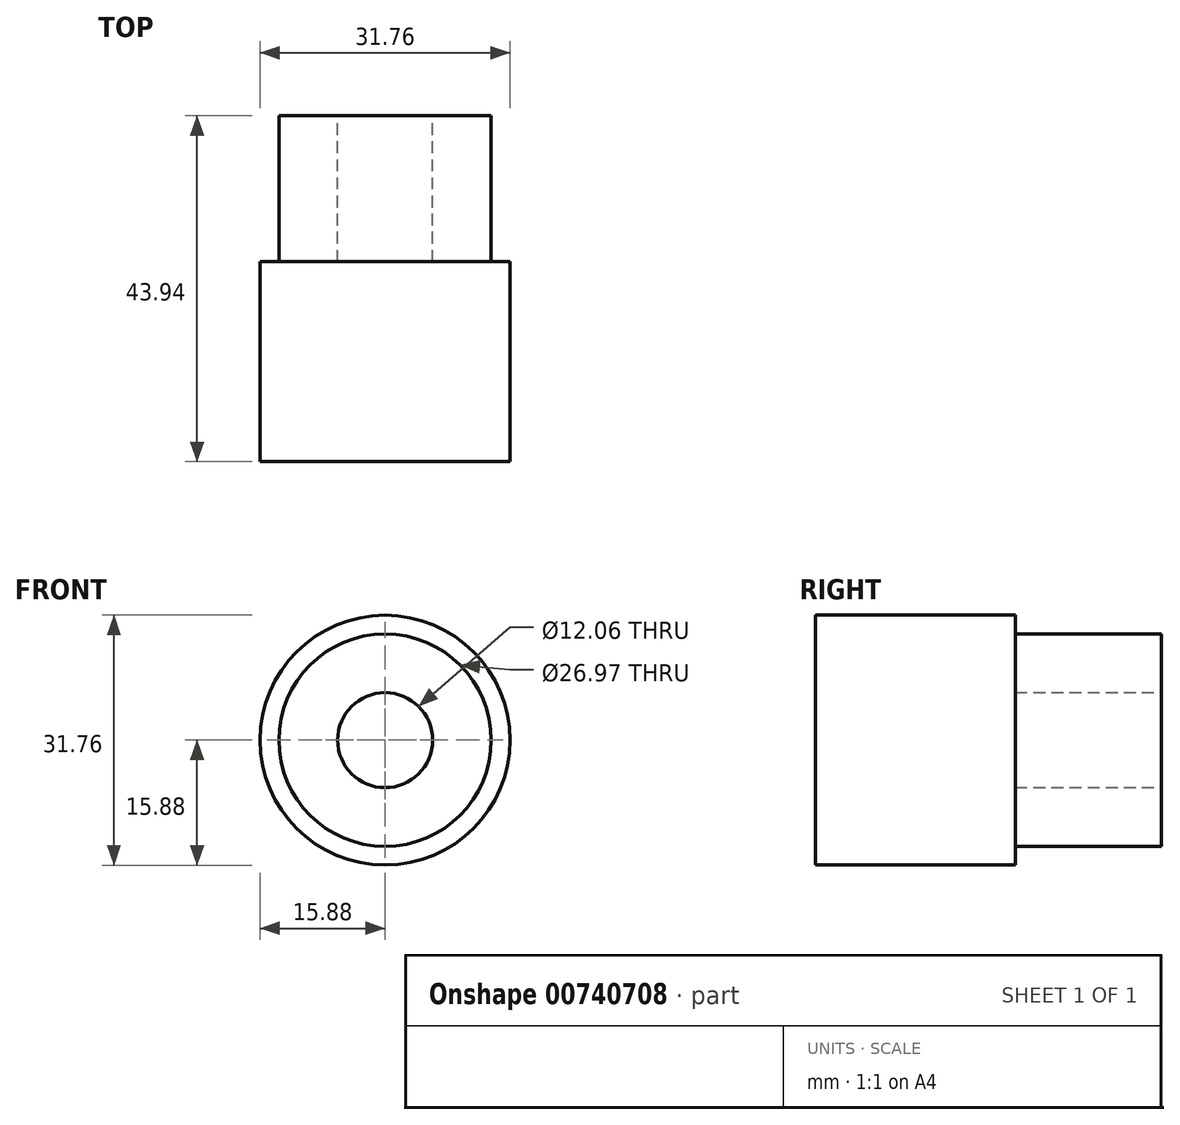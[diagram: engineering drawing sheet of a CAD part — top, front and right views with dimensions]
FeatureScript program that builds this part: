
annotation { "Feature Type Name" : "Feature", "Feature Type Description" : "" }
export const myFeature = defineFeature(function(context is Context, id is Id, definition is map)
    precondition{}
    {
        {
            var Q0;
            Q0=qCreatedBy(makeId("Front.planeOp"),FACE);
            var sketch = newSketch(context, id + "F0", { "sketchPlane" : qUnion([Q0])});
            skCircle(sketch, "E0", {"center": v(0, 0) * mm, "radius": 15.88 * mm});
            skSolve(sketch);
        }
        {
            var Q0;
            Q0=sQuery(id+"F0.wireOp",EDGE,"E0");
            extrude(context, id + "F1", {"bodyType" : ToolBodyType.SURFACE, "surfaceEntities" : qUnion([Q0]), "depth" : 25.4 * mm, "offsetDistance" : 25.4 * mm});
        }
        {
            var Q0;
            Q0=qCreatedBy(makeId("Front.planeOp"),FACE);
            var sketch = newSketch(context, id + "F2", { "sketchPlane" : qUnion([Q0])});
            skCircle(sketch, "E1", {"center": v(0, 0) * mm, "radius": 13.49 * mm});
            skSolve(sketch);
        }
        {
            var Q0;
            Q0=sQuery(id+"F2.wireOp",EDGE,"E1");
            extrude(context, id + "F3", {"bodyType" : ToolBodyType.SURFACE, "surfaceEntities" : qUnion([Q0]), "oppositeDirection" : true, "depth" : 18.54 * mm, "offsetDistance" : 25.4 * mm});
        }
        {
            var Q0;
            Q0=qCreatedBy(makeId("Front.planeOp"),FACE);
            var sketch = newSketch(context, id + "F4", { "sketchPlane" : qUnion([Q0])});
            skCircle(sketch, "E2", {"center": v(0, 0) * mm, "radius": 6.03 * mm});
            skSolve(sketch);
        }
        {
            var Q0;
            Q0=sQuery(id+"F4.wireOp",EDGE,"E2");
            extrude(context, id + "F5", {"bodyType" : ToolBodyType.SURFACE, "surfaceEntities" : qUnion([Q0]), "oppositeDirection" : true, "depth" : 18.54 * mm, "offsetDistance" : 25.4 * mm});
        }
    });
